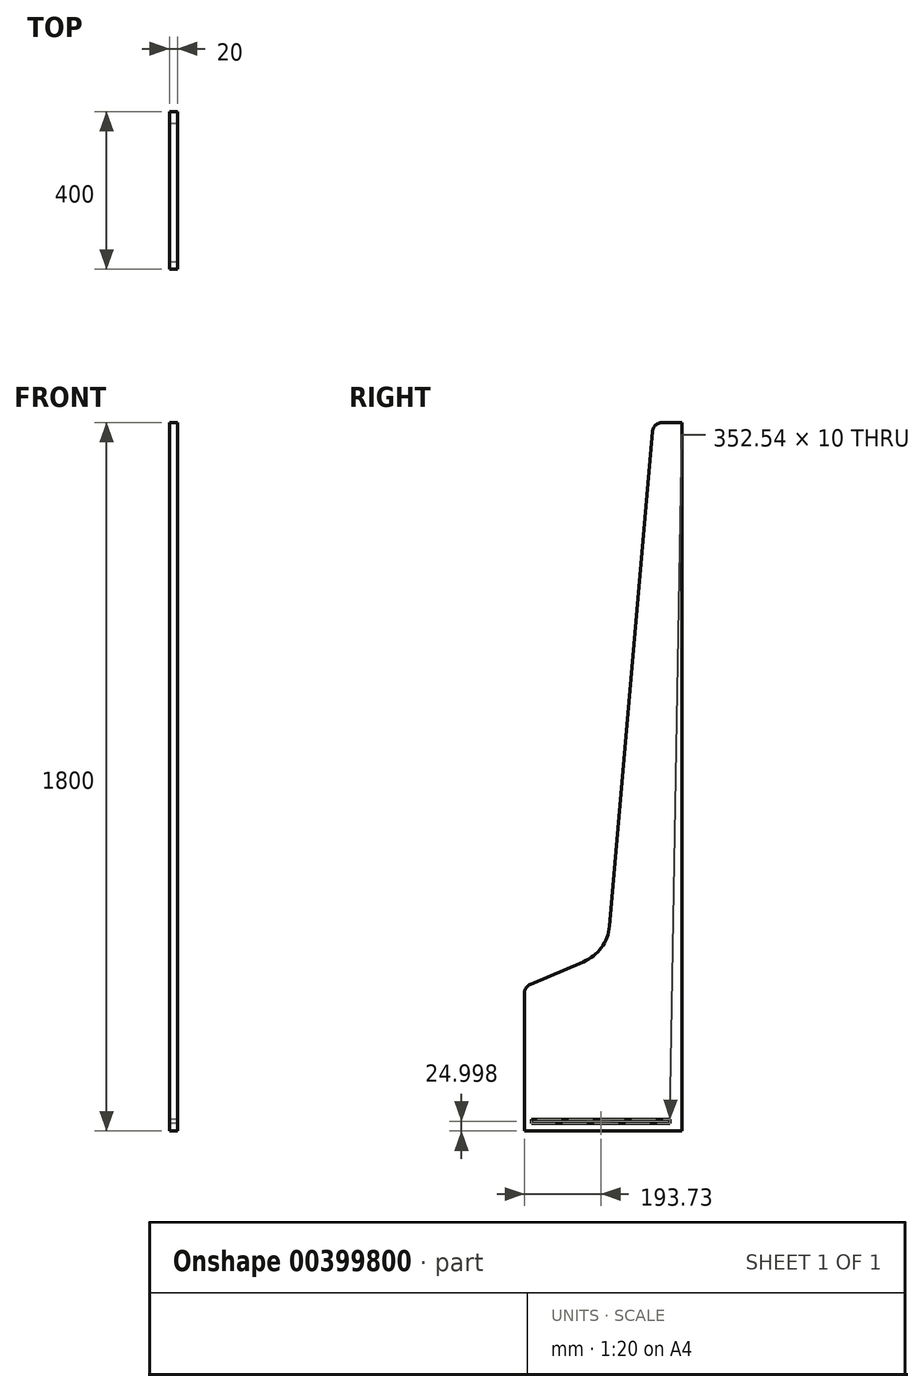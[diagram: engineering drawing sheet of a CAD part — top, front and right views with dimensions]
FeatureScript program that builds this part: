
annotation { "Feature Type Name" : "Feature", "Feature Type Description" : "" }
export const myFeature = defineFeature(function(context is Context, id is Id, definition is map)
    precondition{}
    {
        {
            var Q0;
            Q0=qCreatedBy(makeId("Right.planeOp"),FACE);
            var sketch = newSketch(context, id + "F0", { "sketchPlane" : qUnion([Q0])});
            skLineSegment(sketch, "E0", {"start": v(0, 243.64) * mm, "end": v(0, -1556.36) * mm});
            skArc(sketch, "E1.MirrorCS", {"start": v(-400, -1206.36) * mm, "mid": v(-395.84, -1192.55) * mm, "end": v(-384.74, -1183.34) * mm});
            skArc(sketch, "E2.MirrorCS", {"start": v(-250, -1126.36) * mm, "mid": v(-204.47, -1090.21) * mm, "end": v(-184.12, -1035.76) * mm});
            skLineSegment(sketch, "E3.MirrorCS", {"start": v(-384.74, -1183.34) * mm, "end": v(-250, -1126.36) * mm});
            skLineSegment(sketch, "E4.MirrorCS", {"start": v(-400, -1556.36) * mm, "end": v(-400, -1206.36) * mm});
            skLineSegment(sketch, "E5.MirrorCS", {"start": v(0, -1556.36) * mm, "end": v(-400, -1556.36) * mm});
            skLineSegment(sketch, "E6.MirrorCS", {"start": v(-50, 243.64) * mm, "end": v(0, 243.64) * mm});
            skLineSegment(sketch, "E7.MirrorCS", {"start": v(-184.12, -1035.76) * mm, "end": v(-74.9, 220.8) * mm});
            skArc(sketch, "E8.MirrorCS", {"start": v(-74.9, 220.8) * mm, "mid": v(-66.9, 237.06) * mm, "end": v(-50, 243.64) * mm});
            skLineSegment(sketch, "E9", {"start": v(-163.03, -617.73) * mm, "end": v(-163.03, 182.67) * mm});
            skLineSegment(sketch, "E10.bottom", {"start": v(-10, 233.64) * mm, "end": v(-30, 233.64) * mm});
            skLineSegment(sketch, "E10.top", {"start": v(-10, -1536.36) * mm, "end": v(-30, -1536.36) * mm});
            skLineSegment(sketch, "E10.left", {"start": v(-10, 233.64) * mm, "end": v(-10, -1536.36) * mm});
            skLineSegment(sketch, "E10.right", {"start": v(-30, 233.64) * mm, "end": v(-30, -1536.36) * mm});
            skLineSegment(sketch, "E11.bottom", {"start": v(-30, -1536.36) * mm, "end": v(-382.54, -1536.36) * mm});
            skLineSegment(sketch, "E11.top", {"start": v(-30, -1526.36) * mm, "end": v(-382.54, -1526.36) * mm});
            skLineSegment(sketch, "E11.left", {"start": v(-30, -1536.36) * mm, "end": v(-30, -1526.36) * mm});
            skLineSegment(sketch, "E11.right", {"start": v(-382.54, -1536.36) * mm, "end": v(-382.54, -1526.36) * mm});
            skSolve(sketch);
        }
        {
            var Q0;
            Q0=makeQuery(id+"F0.imprint","IMPRINT",FACE,{"disambiguationData":[TD([[makeQuery(id+"F0.imprint","IMPRINT",EDGE,{"derivedFrom":sQuery(id+"F0.wireOp",EDGE,"E0")}),-1.0]])]});
            var Q1;
            Q1=makeQuery(id+"F0.imprint","IMPRINT",FACE,{"disambiguationData":[TD([[makeQuery(id+"F0.imprint","IMPRINT",EDGE,{"derivedFrom":sQuery(id+"F0.wireOp",EDGE,"E10.bottom")}),1.0]])]});
            extrude(context, id + "F1", {"entities" : qUnion([Q0, Q1]), "depth" : 20 * mm});
        }
    });
